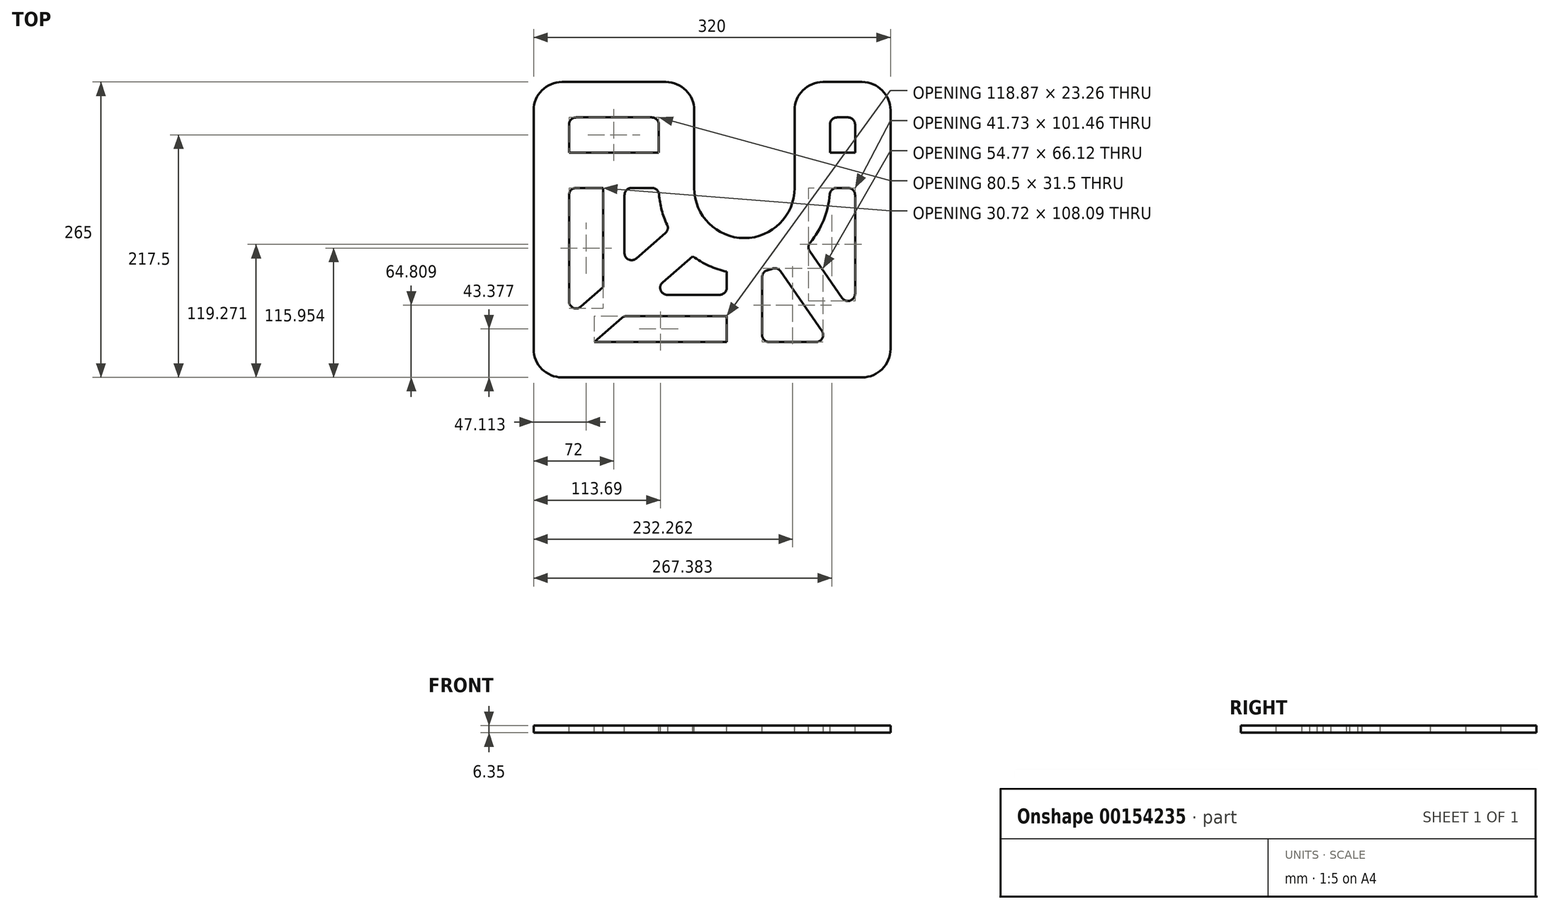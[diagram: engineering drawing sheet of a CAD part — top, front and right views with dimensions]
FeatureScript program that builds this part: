
annotation { "Feature Type Name" : "Feature", "Feature Type Description" : "" }
export const myFeature = defineFeature(function(context is Context, id is Id, definition is map)
    precondition{}
    {
        {
            var Q0;
            Q0=qCreatedBy(makeId("Top.planeOp"),FACE);
            var sketch = newSketch(context, id + "F0", { "sketchPlane" : qUnion([Q0])});
            skLineSegment(sketch, "E0", {"start": v(-189, 95) * mm, "end": v(-189, -170) * mm});
            skLineSegment(sketch, "E1", {"start": v(-189, -170) * mm, "end": v(131, -170) * mm});
            skLineSegment(sketch, "E2", {"start": v(131, -170) * mm, "end": v(131, 95) * mm});
            skLineSegment(sketch, "E3", {"start": v(131, 95) * mm, "end": v(45, 95) * mm});
            skLineSegment(sketch, "E4", {"start": v(45, 95) * mm, "end": v(45, 0) * mm});
            skArc(sketch, "E5", {"start": v(-45, 0) * mm, "mid": v(0, -45) * mm, "end": v(45, 0) * mm});
            skLineSegment(sketch, "E6", {"start": v(-45, 0) * mm, "end": v(-45, 95) * mm});
            skLineSegment(sketch, "E7", {"start": v(-45, 95) * mm, "end": v(-189, 95) * mm});
            skPoint(sketch, "E8.visualSharp", {"position": v(-45, 95) * mm});
            skPoint(sketch, "E9.visualSharp", {"position": v(-189, 95) * mm});
            skPoint(sketch, "E10.visualSharp", {"position": v(-189, -170) * mm});
            skPoint(sketch, "E11.visualSharp", {"position": v(131, -170) * mm});
            skPoint(sketch, "E12.visualSharp", {"position": v(131, 95) * mm});
            skPoint(sketch, "E13.visualSharp", {"position": v(45, 95) * mm});
            skArc(sketch, "E14.0", {"start": v(-76.75, 0) * mm, "mid": v(0, -76.75) * mm, "end": v(76.75, 0) * mm});
            skLineSegment(sketch, "E14.1", {"start": v(76.75, 63.25) * mm, "end": v(76.75, 0) * mm});
            skLineSegment(sketch, "E14.2", {"start": v(-76.75, 0) * mm, "end": v(-76.75, 63.25) * mm});
            skLineSegment(sketch, "E14.3", {"start": v(99.25, 63.25) * mm, "end": v(76.75, 63.25) * mm});
            skLineSegment(sketch, "E14.4", {"start": v(-76.75, 63.25) * mm, "end": v(-157.25, 63.25) * mm});
            skLineSegment(sketch, "E14.5", {"start": v(-157.25, 63.25) * mm, "end": v(-157.25, -138.25) * mm});
            skLineSegment(sketch, "E14.6", {"start": v(-157.25, -138.25) * mm, "end": v(99.25, -138.25) * mm});
            skLineSegment(sketch, "E14.7", {"start": v(99.25, -138.25) * mm, "end": v(99.25, 63.25) * mm});
            skSolve(sketch);
        }
        {
            var Q0;
            Q0 = qSketchRegion(id + "F0", true);
            extrude(context, id + "F1", {"entities" : qUnion([Q0]), "oppositeDirection" : true, "depth" : 6.35 * mm});
        }
        {
            var Q0;
            Q0=makeQuery(id+"F1.opExtrude","CAP_FACE",FACE,{"disambiguationData":[OSD([sQuery(id+"F0.wireOp",EDGE,"E0"),sQuery(id+"F0.wireOp",EDGE,"E1"),sQuery(id+"F0.wireOp",EDGE,"E2"),sQuery(id+"F0.wireOp",EDGE,"E3"),sQuery(id+"F0.wireOp",EDGE,"E4"),sQuery(id+"F0.wireOp",EDGE,"E5"),sQuery(id+"F0.wireOp",EDGE,"E6"),sQuery(id+"F0.wireOp",EDGE,"E7"),sQuery(id+"F0.wireOp",EDGE,"E14.0"),sQuery(id+"F0.wireOp",EDGE,"E14.1"),sQuery(id+"F0.wireOp",EDGE,"E14.2"),sQuery(id+"F0.wireOp",EDGE,"E14.3"),sQuery(id+"F0.wireOp",EDGE,"E14.4"),sQuery(id+"F0.wireOp",EDGE,"E14.5"),sQuery(id+"F0.wireOp",EDGE,"E14.6"),sQuery(id+"F0.wireOp",EDGE,"E14.7")])],"isStart":true});
            var sketch = newSketch(context, id + "F2", { "sketchPlane" : qUnion([Q0])});
            skLineSegment(sketch, "E15.bottom", {"start": v(-15.88, -75.1) * mm, "end": v(15.88, -75.1) * mm});
            skLineSegment(sketch, "E15.top", {"start": v(-15.87, -138.25) * mm, "end": v(15.88, -138.25) * mm});
            skLineSegment(sketch, "E15.left", {"start": v(-15.88, -75.1) * mm, "end": v(-15.87, -138.25) * mm});
            skLineSegment(sketch, "E15.right", {"start": v(15.88, -75.1) * mm, "end": v(15.88, -138.25) * mm});
            skLineSegment(sketch, "E16.bottom", {"start": v(-76.75, 0) * mm, "end": v(-157.25, 0) * mm});
            skLineSegment(sketch, "E16.top", {"start": v(-76.75, 31.75) * mm, "end": v(-157.25, 31.75) * mm});
            skLineSegment(sketch, "E16.left", {"start": v(-76.75, 0) * mm, "end": v(-76.75, 31.75) * mm});
            skLineSegment(sketch, "E16.right", {"start": v(-157.25, 0) * mm, "end": v(-157.25, 31.75) * mm});
            skLineSegment(sketch, "E17.bottom", {"start": v(76.75, 0) * mm, "end": v(99.25, 0) * mm});
            skLineSegment(sketch, "E17.top", {"start": v(76.75, 31.75) * mm, "end": v(99.25, 31.75) * mm});
            skLineSegment(sketch, "E17.left", {"start": v(76.75, 0) * mm, "end": v(76.75, 31.75) * mm});
            skLineSegment(sketch, "E17.right", {"start": v(99.25, 0) * mm, "end": v(99.25, 31.75) * mm});
            skLineSegment(sketch, "E18", {"start": v(-67.07, -37.3) * mm, "end": v(-157.25, -115.75) * mm});
            skLineSegment(sketch, "E19", {"start": v(-157.25, -115.75) * mm, "end": v(-157.25, -138.25) * mm});
            skLineSegment(sketch, "E20", {"start": v(-157.25, -138.25) * mm, "end": v(-134.75, -138.25) * mm});
            skLineSegment(sketch, "E21", {"start": v(-134.75, -138.25) * mm, "end": v(-46.24, -61.26) * mm});
            skLineSegment(sketch, "E22", {"start": v(-46.24, -61.26) * mm, "end": v(-67.07, -37.3) * mm});
            skLineSegment(sketch, "E23", {"start": v(29.7, -70.77) * mm, "end": v(76.43, -138.25) * mm});
            skLineSegment(sketch, "E24", {"start": v(76.43, -138.25) * mm, "end": v(99.25, -138.25) * mm});
            skLineSegment(sketch, "E25", {"start": v(99.25, -138.25) * mm, "end": v(99.25, -115.43) * mm});
            skLineSegment(sketch, "E26", {"start": v(99.25, -115.43) * mm, "end": v(55.8, -52.7) * mm});
            skLineSegment(sketch, "E27", {"start": v(55.8, -52.7) * mm, "end": v(29.7, -70.77) * mm});
            skSolve(sketch);
        }
        {
            var Q0;
            Q0 = qSketchRegion(id + "F2", true);
            extrude(context, id + "F3", {"entities" : qUnion([Q0]), "operationType" : NewBodyOperationType.ADD, "oppositeDirection" : true, "depth" : 6.35 * mm});
        }
        {
            var Q0;
            Q0=makeQuery(id+"F3.boolean.opBoolean","MERGE",FACE,{"derivedFrom":[makeQuery(id+"F1.opExtrude","CAP_FACE",FACE,{"disambiguationData":[OSD([sQuery(id+"F0.wireOp",EDGE,"E0"),sQuery(id+"F0.wireOp",EDGE,"E1"),sQuery(id+"F0.wireOp",EDGE,"E2"),sQuery(id+"F0.wireOp",EDGE,"E3"),sQuery(id+"F0.wireOp",EDGE,"E4"),sQuery(id+"F0.wireOp",EDGE,"E5"),sQuery(id+"F0.wireOp",EDGE,"E6"),sQuery(id+"F0.wireOp",EDGE,"E7"),sQuery(id+"F0.wireOp",EDGE,"E14.0"),sQuery(id+"F0.wireOp",EDGE,"E14.1"),sQuery(id+"F0.wireOp",EDGE,"E14.2"),sQuery(id+"F0.wireOp",EDGE,"E14.3"),sQuery(id+"F0.wireOp",EDGE,"E14.4"),sQuery(id+"F0.wireOp",EDGE,"E14.5"),sQuery(id+"F0.wireOp",EDGE,"E14.6"),sQuery(id+"F0.wireOp",EDGE,"E14.7")])],"isStart":true}),makeQuery(id+"F3.opExtrude","CAP_FACE",FACE,{"disambiguationData":[OSD([sQuery(id+"F2.wireOp",EDGE,"E15.bottom"),sQuery(id+"F2.wireOp",EDGE,"E15.top"),sQuery(id+"F2.wireOp",EDGE,"E15.left"),sQuery(id+"F2.wireOp",EDGE,"E15.right")])],"isStart":true}),makeQuery(id+"F3.opExtrude","CAP_FACE",FACE,{"disambiguationData":[OSD([sQuery(id+"F2.wireOp",EDGE,"E16.bottom"),sQuery(id+"F2.wireOp",EDGE,"E16.top"),sQuery(id+"F2.wireOp",EDGE,"E16.left"),sQuery(id+"F2.wireOp",EDGE,"E16.right")])],"isStart":true}),makeQuery(id+"F3.opExtrude","CAP_FACE",FACE,{"disambiguationData":[OSD([sQuery(id+"F2.wireOp",EDGE,"E17.bottom"),sQuery(id+"F2.wireOp",EDGE,"E17.top"),sQuery(id+"F2.wireOp",EDGE,"E17.left"),sQuery(id+"F2.wireOp",EDGE,"E17.right")])],"isStart":true}),makeQuery(id+"F3.opExtrude","CAP_FACE",FACE,{"disambiguationData":[OSD([sQuery(id+"F2.wireOp",EDGE,"E18"),sQuery(id+"F2.wireOp",EDGE,"E19"),sQuery(id+"F2.wireOp",EDGE,"E20"),sQuery(id+"F2.wireOp",EDGE,"E21"),sQuery(id+"F2.wireOp",EDGE,"E22")])],"isStart":true}),makeQuery(id+"F3.opExtrude","CAP_FACE",FACE,{"disambiguationData":[OSD([sQuery(id+"F2.wireOp",EDGE,"E23"),sQuery(id+"F2.wireOp",EDGE,"E24"),sQuery(id+"F2.wireOp",EDGE,"E25"),sQuery(id+"F2.wireOp",EDGE,"E26"),sQuery(id+"F2.wireOp",EDGE,"E27")])],"isStart":true})]});
            var sketch = newSketch(context, id + "F4", { "sketchPlane" : qUnion([Q0])});
            skLineSegment(sketch, "E28.bottom", {"start": v(-126.53, 0) * mm, "end": v(-107.47, 0) * mm});
            skLineSegment(sketch, "E28.top", {"start": v(-126.53, -89.02) * mm, "end": v(-107.47, -89.02) * mm});
            skLineSegment(sketch, "E28.left", {"start": v(-126.53, 0) * mm, "end": v(-126.53, -89.02) * mm});
            skLineSegment(sketch, "E28.right", {"start": v(-107.47, 0) * mm, "end": v(-107.47, -89.02) * mm});
            skLineSegment(sketch, "E29.bottom", {"start": v(-15.88, -115) * mm, "end": v(-108.01, -115) * mm});
            skLineSegment(sketch, "E29.top", {"start": v(-15.88, -95.94) * mm, "end": v(-108.01, -95.94) * mm});
            skLineSegment(sketch, "E29.left", {"start": v(-15.88, -115) * mm, "end": v(-15.88, -95.94) * mm});
            skLineSegment(sketch, "E29.right", {"start": v(-108.01, -115) * mm, "end": v(-108.01, -95.94) * mm});
            skSolve(sketch);
        }
        {
            var Q0;
            Q0 = qSketchRegion(id + "F4", true);
            extrude(context, id + "F5", {"entities" : qUnion([Q0]), "operationType" : NewBodyOperationType.ADD, "oppositeDirection" : true, "depth" : 6.35 * mm});
        }
        {
            var Q0;
            Q0=makeQuery(id+"F1.opExtrude","SWEPT_EDGE",EDGE,{"disambiguationData":[OSD([sQuery(id+"F0.wireOp",EDGE,"E0"),sQuery(id+"F0.wireOp",EDGE,"E7")])]});
            var Q1;
            Q1=makeQuery(id+"F1.opExtrude","SWEPT_EDGE",EDGE,{"disambiguationData":[OSD([sQuery(id+"F0.wireOp",EDGE,"E0"),sQuery(id+"F0.wireOp",EDGE,"E1")])]});
            var Q2;
            Q2=makeQuery(id+"F1.opExtrude","SWEPT_EDGE",EDGE,{"disambiguationData":[OSD([sQuery(id+"F0.wireOp",EDGE,"E1"),sQuery(id+"F0.wireOp",EDGE,"E2")])]});
            var Q3;
            Q3=makeQuery(id+"F1.opExtrude","SWEPT_EDGE",EDGE,{"disambiguationData":[OSD([sQuery(id+"F0.wireOp",EDGE,"E2"),sQuery(id+"F0.wireOp",EDGE,"E3")])]});
            var Q4;
            Q4=makeQuery(id+"F1.opExtrude","SWEPT_EDGE",EDGE,{"disambiguationData":[OSD([sQuery(id+"F0.wireOp",EDGE,"E3"),sQuery(id+"F0.wireOp",EDGE,"E4")])]});
            var Q5;
            Q5=makeQuery(id+"F1.opExtrude","SWEPT_EDGE",EDGE,{"disambiguationData":[OSD([sQuery(id+"F0.wireOp",EDGE,"E6"),sQuery(id+"F0.wireOp",EDGE,"E7")])]});
            fillet(context, id + "F6", {"entities" : qUnion([Q0, Q1, Q2, Q3, Q4, Q5]), "radius" : 25.4 * mm, "tangentPropagation" : true, "allowEdgeOverflow" : false});
        }
        {
            var Q0;
            Q0=makeQuery(id+"F1.opExtrude","SWEPT_EDGE",EDGE,{"disambiguationData":[OSD([sQuery(id+"F0.wireOp",EDGE,"E14.1"),sQuery(id+"F0.wireOp",EDGE,"E14.3")])]});
            var Q1;
            Q1=makeQuery(id+"F1.opExtrude","SWEPT_EDGE",EDGE,{"disambiguationData":[OSD([sQuery(id+"F0.wireOp",EDGE,"E14.3"),sQuery(id+"F0.wireOp",EDGE,"E14.7")])]});
            var Q2;
            Q2=makeQuery(id+"F3.opExtrude","SWEPT_EDGE",EDGE,{"disambiguationData":[OSD([sQuery(id+"F0.wireOp",EDGE,"E14.1"),sQuery(id+"F2.wireOp",EDGE,"E17.top"),sQuery(id+"F2.wireOp",EDGE,"E17.left")])]});
            var Q3;
            Q3=makeQuery(id+"F3.opExtrude","SWEPT_EDGE",EDGE,{"disambiguationData":[OSD([sQuery(id+"F0.wireOp",EDGE,"E14.7"),sQuery(id+"F2.wireOp",EDGE,"E17.top"),sQuery(id+"F2.wireOp",EDGE,"E17.right")])]});
            var Q4;
            Q4=makeQuery(id+"F3.opExtrude","SWEPT_EDGE",EDGE,{"disambiguationData":[OSD([sQuery(id+"F0.wireOp",EDGE,"E14.0"),sQuery(id+"F2.wireOp",EDGE,"E26"),sQuery(id+"F2.wireOp",EDGE,"E27")])]});
            var Q5;
            Q5=makeQuery(id+"F3.opExtrude","SWEPT_EDGE",EDGE,{"disambiguationData":[OSD([sQuery(id+"F0.wireOp",EDGE,"E14.5"),sQuery(id+"F2.wireOp",EDGE,"E16.top"),sQuery(id+"F2.wireOp",EDGE,"E16.right")])]});
            var Q6;
            Q6=makeQuery(id+"F3.opExtrude","SWEPT_EDGE",EDGE,{"disambiguationData":[OSD([sQuery(id+"F0.wireOp",EDGE,"E14.6"),sQuery(id+"F2.wireOp",EDGE,"E20"),sQuery(id+"F2.wireOp",EDGE,"E21")])]});
            var Q7;
            Q7=makeQuery(id+"F5.boolean.opBoolean","INTERSECT",EDGE,{"derivedFrom":[makeQuery(id+"F3.opExtrude","SWEPT_FACE",FACE,{"disambiguationData":[OSD([sQuery(id+"F2.wireOp",EDGE,"E21")])]}),makeQuery(id+"F5.opExtrude","SWEPT_FACE",FACE,{"disambiguationData":[OSD([sQuery(id+"F4.wireOp",EDGE,"E29.top")])]})]});
            var Q8;
            Q8=makeQuery(id+"F3.opExtrude","SWEPT_EDGE",EDGE,{"disambiguationData":[OSD([sQuery(id+"F0.wireOp",EDGE,"E14.6"),sQuery(id+"F2.wireOp",EDGE,"E15.top"),sQuery(id+"F2.wireOp",EDGE,"E15.right")])]});
            var Q9;
            Q9=makeQuery(id+"F3.opExtrude","SWEPT_EDGE",EDGE,{"disambiguationData":[OSD([sQuery(id+"F0.wireOp",EDGE,"E14.5"),sQuery(id+"F2.wireOp",EDGE,"E16.bottom"),sQuery(id+"F2.wireOp",EDGE,"E16.right")])]});
            var Q10;
            Q10=makeQuery(id+"F1.opExtrude","SWEPT_EDGE",EDGE,{"disambiguationData":[OSD([sQuery(id+"F0.wireOp",EDGE,"E14.4"),sQuery(id+"F0.wireOp",EDGE,"E14.5")])]});
            var Q11;
            Q11=makeQuery(id+"F5.opExtrude","SWEPT_EDGE",EDGE,{"disambiguationData":[OSD([sQuery(id+"F2.wireOp",EDGE,"E16.bottom"),sQuery(id+"F4.wireOp",EDGE,"E28.bottom"),sQuery(id+"F4.wireOp",EDGE,"E28.right")])]});
            var Q12;
            Q12=makeQuery(id+"F3.opExtrude","SWEPT_EDGE",EDGE,{"disambiguationData":[OSD([sQuery(id+"F0.wireOp",EDGE,"E14.0"),sQuery(id+"F2.wireOp",EDGE,"E21"),sQuery(id+"F2.wireOp",EDGE,"E22")])]});
            var Q13;
            Q13=makeQuery(id+"F5.opExtrude","SWEPT_EDGE",EDGE,{"disambiguationData":[OSD([sQuery(id+"F2.wireOp",EDGE,"E21"),sQuery(id+"F4.wireOp",EDGE,"E29.bottom"),sQuery(id+"F4.wireOp",EDGE,"E29.right")])]});
            var Q14;
            Q14=makeQuery(id+"F3.opExtrude","SWEPT_EDGE",EDGE,{"disambiguationData":[OSD([sQuery(id+"F0.wireOp",EDGE,"E14.0"),sQuery(id+"F2.wireOp",EDGE,"E15.bottom"),sQuery(id+"F2.wireOp",EDGE,"E15.right")])]});
            var Q15;
            {var subQ0=sQuery(id+"F0.wireOp",EDGE,"E14.0");Q15=makeQuery(id+"F3.boolean.opBoolean","MERGE",EDGE,{"derivedFrom":[makeQuery(id+"F1.opExtrude","SWEPT_EDGE",EDGE,{"disambiguationData":[OSD([subQ0,sQuery(id+"F0.wireOp",EDGE,"E14.1")])]}),makeQuery(id+"F3.opExtrude","SWEPT_EDGE",EDGE,{"disambiguationData":[OSD([subQ0,sQuery(id+"F2.wireOp",EDGE,"E17.bottom"),sQuery(id+"F2.wireOp",EDGE,"E17.left")])]})]});}
            var Q16;
            Q16=makeQuery(id+"F3.opExtrude","SWEPT_EDGE",EDGE,{"disambiguationData":[OSD([sQuery(id+"F0.wireOp",EDGE,"E14.2"),sQuery(id+"F2.wireOp",EDGE,"E16.top"),sQuery(id+"F2.wireOp",EDGE,"E16.left")])]});
            var Q17;
            Q17=makeQuery(id+"F3.opExtrude","SWEPT_EDGE",EDGE,{"disambiguationData":[OSD([sQuery(id+"F0.wireOp",EDGE,"E14.0"),sQuery(id+"F2.wireOp",EDGE,"E18"),sQuery(id+"F2.wireOp",EDGE,"E22")])]});
            var Q18;
            Q18=makeQuery(id+"F5.opExtrude","SWEPT_EDGE",EDGE,{"disambiguationData":[OSD([sQuery(id+"F2.wireOp",EDGE,"E15.left"),sQuery(id+"F4.wireOp",EDGE,"E29.top"),sQuery(id+"F4.wireOp",EDGE,"E29.left")])]});
            var Q19;
            Q19=makeQuery(id+"F3.opExtrude","SWEPT_EDGE",EDGE,{"disambiguationData":[OSD([sQuery(id+"F0.wireOp",EDGE,"E14.6"),sQuery(id+"F2.wireOp",EDGE,"E23"),sQuery(id+"F2.wireOp",EDGE,"E24")])]});
            var Q20;
            Q20=makeQuery(id+"F3.opExtrude","SWEPT_EDGE",EDGE,{"disambiguationData":[OSD([sQuery(id+"F0.wireOp",EDGE,"E14.6"),sQuery(id+"F2.wireOp",EDGE,"E15.top"),sQuery(id+"F2.wireOp",EDGE,"E15.left")])]});
            var Q21;
            Q21=makeQuery(id+"F5.opExtrude","SWEPT_EDGE",EDGE,{"disambiguationData":[OSD([sQuery(id+"F2.wireOp",EDGE,"E18"),sQuery(id+"F4.wireOp",EDGE,"E28.top"),sQuery(id+"F4.wireOp",EDGE,"E28.left")])]});
            var Q22;
            Q22=makeQuery(id+"F5.boolean.opBoolean","INTERSECT",EDGE,{"derivedFrom":[makeQuery(id+"F3.opExtrude","SWEPT_FACE",FACE,{"disambiguationData":[OSD([sQuery(id+"F2.wireOp",EDGE,"E18")])]}),makeQuery(id+"F5.opExtrude","SWEPT_FACE",FACE,{"disambiguationData":[OSD([sQuery(id+"F4.wireOp",EDGE,"E28.right")])]})]});
            var Q23;
            Q23=makeQuery(id+"F3.opExtrude","SWEPT_EDGE",EDGE,{"disambiguationData":[OSD([sQuery(id+"F0.wireOp",EDGE,"E14.5"),sQuery(id+"F2.wireOp",EDGE,"E18"),sQuery(id+"F2.wireOp",EDGE,"E19")])]});
            var Q24;
            Q24=makeQuery(id+"F3.opExtrude","SWEPT_EDGE",EDGE,{"disambiguationData":[OSD([sQuery(id+"F0.wireOp",EDGE,"E14.7"),sQuery(id+"F2.wireOp",EDGE,"E17.bottom"),sQuery(id+"F2.wireOp",EDGE,"E17.right")])]});
            var Q25;
            Q25=makeQuery(id+"F3.opExtrude","SWEPT_EDGE",EDGE,{"disambiguationData":[OSD([sQuery(id+"F0.wireOp",EDGE,"E14.0"),sQuery(id+"F2.wireOp",EDGE,"E15.bottom"),sQuery(id+"F2.wireOp",EDGE,"E15.left")])]});
            var Q26;
            Q26=makeQuery(id+"F5.opExtrude","SWEPT_EDGE",EDGE,{"disambiguationData":[OSD([sQuery(id+"F2.wireOp",EDGE,"E15.left"),sQuery(id+"F4.wireOp",EDGE,"E29.bottom"),sQuery(id+"F4.wireOp",EDGE,"E29.left")])]});
            var Q27;
            {var subQ0=sQuery(id+"F0.wireOp",EDGE,"E14.0");Q27=makeQuery(id+"F3.boolean.opBoolean","MERGE",EDGE,{"derivedFrom":[makeQuery(id+"F1.opExtrude","SWEPT_EDGE",EDGE,{"disambiguationData":[OSD([subQ0,sQuery(id+"F0.wireOp",EDGE,"E14.2")])]}),makeQuery(id+"F3.opExtrude","SWEPT_EDGE",EDGE,{"disambiguationData":[OSD([subQ0,sQuery(id+"F2.wireOp",EDGE,"E16.bottom"),sQuery(id+"F2.wireOp",EDGE,"E16.left")])]})]});}
            var Q28;
            Q28=makeQuery(id+"F1.opExtrude","SWEPT_EDGE",EDGE,{"disambiguationData":[OSD([sQuery(id+"F0.wireOp",EDGE,"E14.2"),sQuery(id+"F0.wireOp",EDGE,"E14.4")])]});
            var Q29;
            Q29=makeQuery(id+"F3.opExtrude","SWEPT_EDGE",EDGE,{"disambiguationData":[OSD([sQuery(id+"F0.wireOp",EDGE,"E14.0"),sQuery(id+"F2.wireOp",EDGE,"E23"),sQuery(id+"F2.wireOp",EDGE,"E27")])]});
            var Q30;
            Q30=makeQuery(id+"F5.opExtrude","SWEPT_EDGE",EDGE,{"disambiguationData":[OSD([sQuery(id+"F2.wireOp",EDGE,"E16.bottom"),sQuery(id+"F4.wireOp",EDGE,"E28.bottom"),sQuery(id+"F4.wireOp",EDGE,"E28.left")])]});
            var Q31;
            Q31=makeQuery(id+"F3.opExtrude","SWEPT_EDGE",EDGE,{"disambiguationData":[OSD([sQuery(id+"F0.wireOp",EDGE,"E14.7"),sQuery(id+"F2.wireOp",EDGE,"E25"),sQuery(id+"F2.wireOp",EDGE,"E26")])]});
            fillet(context, id + "F7", {"entities" : qUnion([Q0, Q1, Q2, Q3, Q4, Q5, Q6, Q7, Q8, Q9, Q10, Q11, Q12, Q13, Q14, Q15, Q16, Q17, Q18, Q19, Q20, Q21, Q22, Q23, Q24, Q25, Q26, Q27, Q28, Q29, Q30, Q31]), "radius" : 6.35 * mm, "tangentPropagation" : true, "allowEdgeOverflow" : false});
        }
    });
